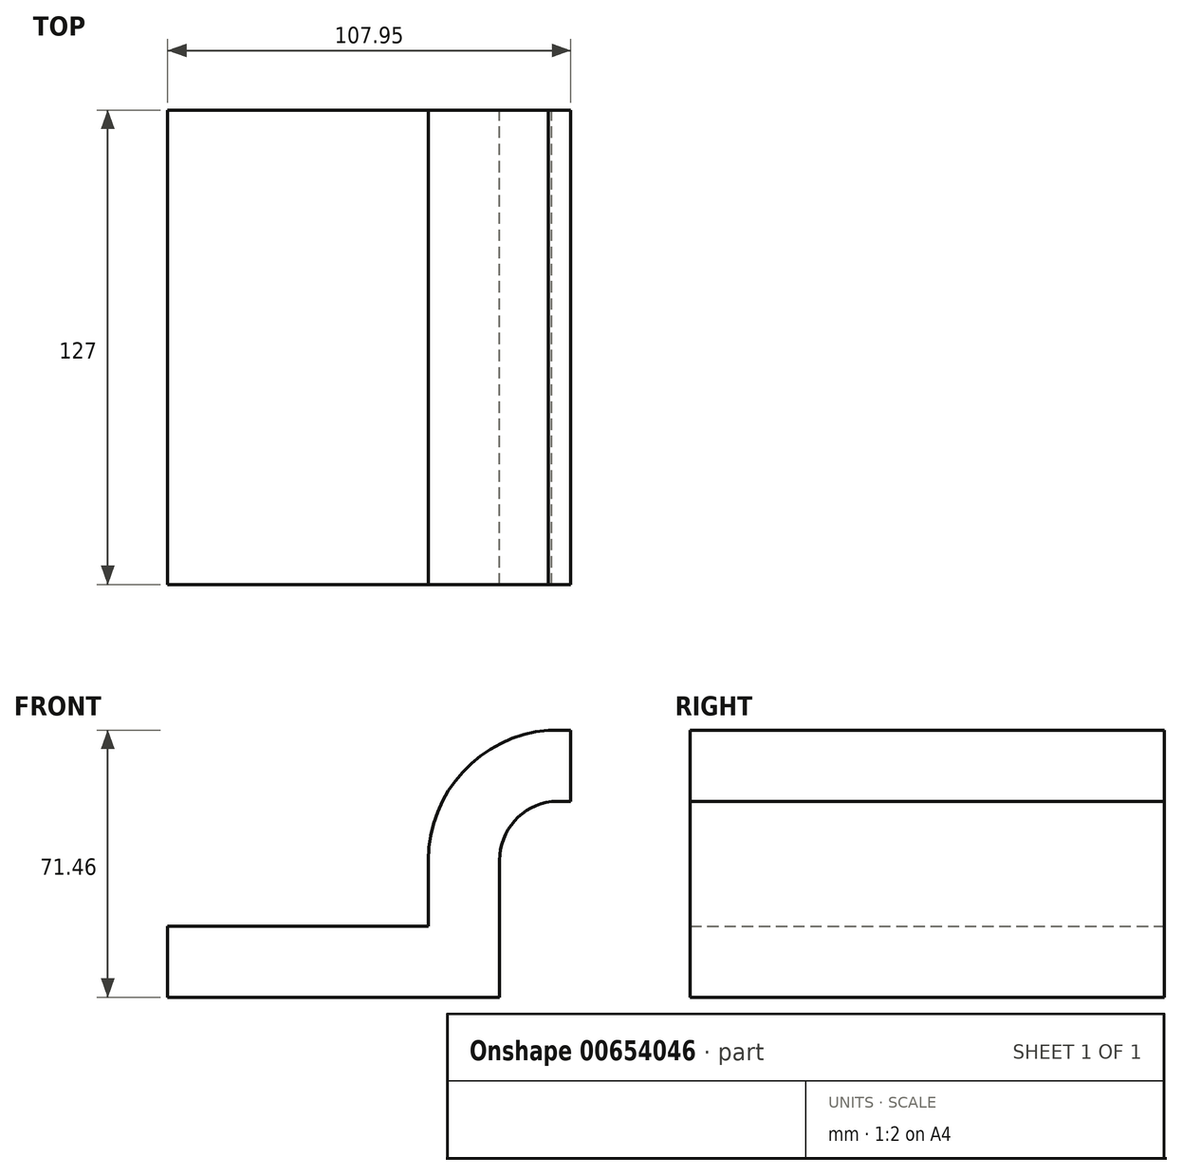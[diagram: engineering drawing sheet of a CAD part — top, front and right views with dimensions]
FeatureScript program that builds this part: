
annotation { "Feature Type Name" : "Feature", "Feature Type Description" : "" }
export const myFeature = defineFeature(function(context is Context, id is Id, definition is map)
    precondition{}
    {
        {
            var Q0;
            Q0=qCreatedBy(makeId("Front.planeOp"),FACE);
            var sketch = newSketch(context, id + "F0", { "sketchPlane" : qUnion([Q0])});
            skLineSegment(sketch, "E0.bottom", {"start": v(44.45, -9.52) * mm, "end": v(-44.45, -9.53) * mm});
            skLineSegment(sketch, "E0.top", {"start": v(44.45, 9.53) * mm, "end": v(-44.45, 9.53) * mm});
            skLineSegment(sketch, "E0.left", {"start": v(44.45, -9.52) * mm, "end": v(44.45, 9.53) * mm});
            skLineSegment(sketch, "E0.right", {"start": v(-44.45, -9.53) * mm, "end": v(-44.45, 9.53) * mm});
            skPoint(sketch, "E0.middle", {"position": v(0, 0) * mm});
            skLineSegment(sketch, "E1.bottom", {"start": v(114.3, 38.1) * mm, "end": v(63.5, 38.1) * mm});
            skLineSegment(sketch, "E1.top", {"start": v(114.3, 66.68) * mm, "end": v(63.5, 66.68) * mm});
            skLineSegment(sketch, "E1.left", {"start": v(114.3, 38.1) * mm, "end": v(114.3, 66.68) * mm});
            skLineSegment(sketch, "E1.right", {"start": v(63.5, 38.1) * mm, "end": v(63.5, 66.68) * mm});
            skPoint(sketch, "E1.middle", {"position": v(88.9, 52.39) * mm});
            skLineSegment(sketch, "E2", {"start": v(44.45, 9.53) * mm, "end": v(44.45, 27.12) * mm});
            skArc(sketch, "E3", {"start": v(44.45, 27.12) * mm, "mid": v(48.44, 37.64) * mm, "end": v(58.4, 42.88) * mm});
            skLineSegment(sketch, "E4", {"start": v(58.4, 42.88) * mm, "end": v(88.9, 42.88) * mm});
            skLineSegment(sketch, "E5.0", {"start": v(57.46, 61.93) * mm, "end": v(88.9, 61.93) * mm});
            skArc(sketch, "E5.1", {"start": v(25.4, 27.12) * mm, "mid": v(34.64, 50.78) * mm, "end": v(57.46, 61.93) * mm});
            skLineSegment(sketch, "E5.2", {"start": v(25.4, 9.53) * mm, "end": v(25.4, 27.12) * mm});
            skLineSegment(sketch, "E6", {"start": v(88.9, 38.1) * mm, "end": v(88.9, 66.68) * mm});
            skFitSpline(sketch, "E7", {"points": [v(-44.45, 9.53) * mm, v(57.46, 61.93) * mm], "startDerivative": vector(3.28, 105.8) * mm, "endDerivative": vector(121.38, 0) * mm});
            skSolve(sketch);
        }
        {
            var Q0;
            Q0=makeQuery(id+"F0.imprint","IMPRINT",FACE,{"disambiguationData":[TD([[makeQuery(id+"F0.imprint","IMPRINT",EDGE,{"derivedFrom":sQuery(id+"F0.wireOp",EDGE,"E5.1")}),1.0]])]});
            var Q1;
            Q1=makeQuery(id+"F0.imprint","IMPRINT",FACE,{"disambiguationData":[TD([[makeQuery(id+"F0.imprint","IMPRINT",EDGE,{"derivedFrom":sQuery(id+"F0.wireOp",EDGE,"E0.bottom")}),-1.0]])]});
            extrude(context, id + "F1", {"entities" : qUnion([Q0, Q1]), "endBound" : BoundingType.SYMMETRIC, "depth" : 127 * mm, "offsetDistance" : 25.4 * mm});
        }
    });
